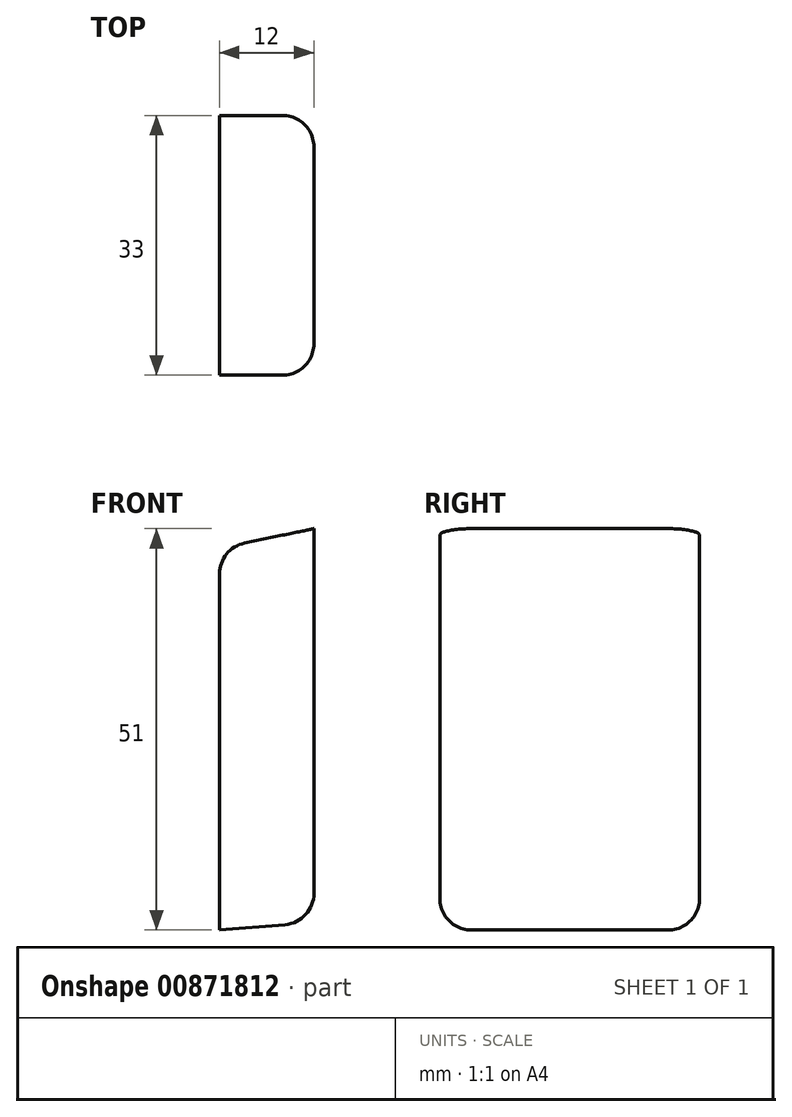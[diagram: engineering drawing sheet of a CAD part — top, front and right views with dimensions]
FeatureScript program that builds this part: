
annotation { "Feature Type Name" : "Feature", "Feature Type Description" : "" }
export const myFeature = defineFeature(function(context is Context, id is Id, definition is map)
    precondition{}
    {
        {
            var Q0;
            Q0=qCreatedBy(makeId("Front.planeOp"),FACE);
            var sketch = newSketch(context, id + "F0", { "sketchPlane" : qUnion([Q0])});
            skLineSegment(sketch, "E0.left", {"start": v(0, 0) * mm, "end": v(0, 50) * mm});
            skLineSegment(sketch, "E0.right", {"start": v(-12, -1) * mm, "end": v(-12, 47.5) * mm});
            skLineSegment(sketch, "E1", {"start": v(0, 50) * mm, "end": v(-12, 47.5) * mm});
            skLineSegment(sketch, "E2", {"start": v(-12, -1) * mm, "end": v(0, 0) * mm});
            skSolve(sketch);
        }
        {
            var Q0;
            Q0 = qSketchRegion(id + "F0", true);
            extrude(context, id + "F1", {"entities" : qUnion([Q0]), "depth" : 33 * mm, "offsetDistance" : 25 * mm});
        }
        {
            var Q0;
            Q0=makeQuery(id+"F1.opExtrude","SWEPT_EDGE",EDGE,{"disambiguationData":[OSD([sQuery(id+"F0.wireOp",EDGE,"E0.right"),sQuery(id+"F0.wireOp",EDGE,"E1")])]});
            var Q1;
            Q1=makeQuery(id+"F1.opExtrude","SWEPT_EDGE",EDGE,{"disambiguationData":[OSD([sQuery(id+"F0.wireOp",EDGE,"E0.left"),sQuery(id+"F0.wireOp",EDGE,"E2")])]});
            var Q2;
            Q2=makeQuery(id+"F1.opExtrude","CAP_EDGE",EDGE,{"disambiguationData":[OSD([sQuery(id+"F0.wireOp",EDGE,"E0.left")])],"isStart":false});
            var Q3;
            Q3=makeQuery(id+"F1.opExtrude","CAP_EDGE",EDGE,{"disambiguationData":[OSD([sQuery(id+"F0.wireOp",EDGE,"E0.left")])],"isStart":true});
            var Q4;
            Q4=makeQuery(id+"F1.opExtrude","CAP_EDGE",EDGE,{"disambiguationData":[OSD([sQuery(id+"F0.wireOp",EDGE,"E2")])],"isStart":false});
            var Q5;
            Q5=makeQuery(id+"F1.opExtrude","CAP_EDGE",EDGE,{"disambiguationData":[OSD([sQuery(id+"F0.wireOp",EDGE,"E2")])],"isStart":true});
            fillet(context, id + "F2", {"entities" : qUnion([Q0, Q1, Q2, Q3, Q4, Q5]), "radius" : 4 * mm, "tangentPropagation" : true, "allowEdgeOverflow" : false});
        }
    });
